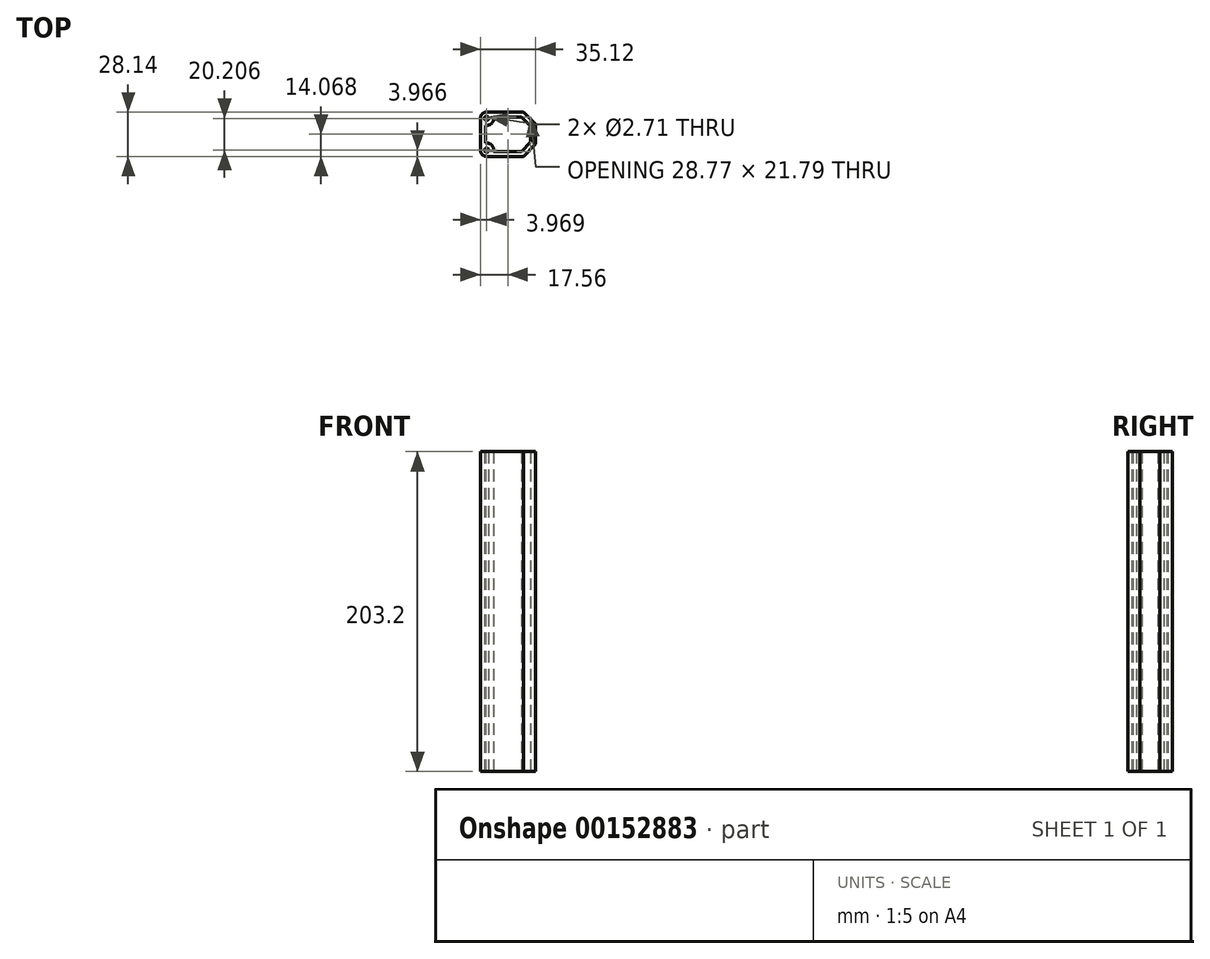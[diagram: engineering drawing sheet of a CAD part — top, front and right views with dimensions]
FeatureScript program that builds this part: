
annotation { "Feature Type Name" : "Feature", "Feature Type Description" : "" }
export const myFeature = defineFeature(function(context is Context, id is Id, definition is map)
    precondition{}
    {
        {
            var Q0;
            Q0=qCreatedBy(makeId("Top.planeOp"),FACE);
            var sketch = newSketch(context, id + "F0", { "sketchPlane" : qUnion([Q0])});
            skCircle(sketch, "E0", {"center": v(3.97, -24.17) * mm, "radius": 1.35 * mm});
            skLineSegment(sketch, "E1", {"start": v(27.4, 0) * mm, "end": v(35.12, -7.72) * mm});
            skLineSegment(sketch, "E2", {"start": v(35.12, -7.72) * mm, "end": v(35.12, -20.42) * mm});
            skLineSegment(sketch, "E3", {"start": v(35.12, -20.42) * mm, "end": v(27.4, -28.14) * mm});
            skCircle(sketch, "E4", {"center": v(3.97, -3.97) * mm, "radius": 1.35 * mm});
            skLineSegment(sketch, "E5", {"start": v(0, 0) * mm, "end": v(0, -28.14) * mm});
            skLineSegment(sketch, "E6", {"start": v(0, 0) * mm, "end": v(27.4, 0) * mm});
            skLineSegment(sketch, "E7", {"start": v(0, -28.14) * mm, "end": v(27.4, -28.14) * mm});
            skLineSegment(sketch, "E8", {"start": v(3.97, 0) * mm, "end": v(3.97, -3.97) * mm, "construction": true});
            skLineSegment(sketch, "E9", {"start": v(3.97, -3.97) * mm, "end": v(3.97, -24.17) * mm, "construction": true});
            skLineSegment(sketch, "E10", {"start": v(3.97, -24.17) * mm, "end": v(3.97, -28.14) * mm, "construction": true});
            skLineSegment(sketch, "E11", {"start": v(3.97, -14.07) * mm, "end": v(0, -14.07) * mm, "construction": true});
            skLineSegment(sketch, "E12", {"start": v(3.97, -14.07) * mm, "end": v(35.12, -14.07) * mm, "construction": true});
            skSolve(sketch);
        }
        {
            var Q0;
            Q0=qSketchRegion(id+"F0",true);
            extrude(context, id + "F1", {"entities" : qUnion([Q0]), "depth" : 203.2 * mm});
        }
        {
            var Q0;
            Q0=makeQuery(id+"F1.opExtrude","CAP_FACE",FACE,{"disambiguationData":[OSD([sQuery(id+"F0.wireOp",EDGE,"XEPYvsBn-YUR1-ND3i-Hliu-0bTDEalwyczA.top"),sQuery(id+"F0.wireOp",EDGE,"XEPYvsBn-YUR1-ND3i-Hliu-0bTDEalwyczA.left"),sQuery(id+"F0.wireOp",EDGE,"XEPYvsBn-YUR1-ND3i-Hliu-0bTDEalwyczA.right"),sQuery(id+"F0.wireOp",EDGE,"xVlwOPhJ-aCTn-OcWs-i2q0-JGyUUewlvZk0"),sQuery(id+"F0.wireOp",EDGE,"mnWjOHlk-ZBn2-aH8g-XAYR-hhn7P80mJV30"),sQuery(id+"F0.wireOp",EDGE,"qWcisiEL-inPN-Vpot-oWrz-rQQv9aT1plas"),sQuery(id+"F0.wireOp",EDGE,"E0"),sQuery(id+"F0.wireOp",EDGE,"wggGBD89-NySP-fc97-dHrN-DnFs8bvNLK9Q"),sQuery(id+"F0.wireOp",EDGE,"5MgdVyr7-DWw4-W8FQ-cNCn-mxH1OUoo9ziA"),sQuery(id+"F0.wireOp",EDGE,"vNbRmb8h-Bngh-6YxP-lEbM-9A7OkrAi9S9c"),sQuery(id+"F0.wireOp",EDGE,"E1"),sQuery(id+"F0.wireOp",EDGE,"E2"),sQuery(id+"F0.wireOp",EDGE,"E3"),sQuery(id+"F0.wireOp",EDGE,"jR9S6iYZ-1zVe-prUs-f2vK-9AuAnzNDGjG4"),sQuery(id+"F0.wireOp",EDGE,"E4"),sQuery(id+"F0.wireOp",EDGE,"pcKUxt8c-gCmA-zyht-Zhnu-jqMgmv6wgrW5")])],"isStart":false});
            shell(context, id + "F2", {"entities" : qUnion([Q0]), "thickness" : 3.17 * mm});
        }
        {
            var Q0;
            Q0=makeQuery(id+"F2.opShell","OFFSET_FACE",FACE,{"disambiguationData":[OSD([sQuery(id+"F0.wireOp",EDGE,"mnWjOHlk-ZBn2-aH8g-XAYR-hhn7P80mJV30"),sQuery(id+"F0.wireOp",EDGE,"qWcisiEL-inPN-Vpot-oWrz-rQQv9aT1plas"),sQuery(id+"F0.wireOp",EDGE,"E0"),sQuery(id+"F0.wireOp",EDGE,"wggGBD89-NySP-fc97-dHrN-DnFs8bvNLK9Q"),sQuery(id+"F0.wireOp",EDGE,"5MgdVyr7-DWw4-W8FQ-cNCn-mxH1OUoo9ziA"),sQuery(id+"F0.wireOp",EDGE,"vNbRmb8h-Bngh-6YxP-lEbM-9A7OkrAi9S9c"),sQuery(id+"F0.wireOp",EDGE,"E1"),sQuery(id+"F0.wireOp",EDGE,"E2"),sQuery(id+"F0.wireOp",EDGE,"E3"),sQuery(id+"F0.wireOp",EDGE,"jR9S6iYZ-1zVe-prUs-f2vK-9AuAnzNDGjG4"),sQuery(id+"F0.wireOp",EDGE,"E4"),sQuery(id+"F0.wireOp",EDGE,"pcKUxt8c-gCmA-zyht-Zhnu-jqMgmv6wgrW5")])]});
            var Q1;
            Q1=makeQuery(id+"F1.opExtrude","CAP_FACE",FACE,{"disambiguationData":[OSD([sQuery(id+"F0.wireOp",EDGE,"mnWjOHlk-ZBn2-aH8g-XAYR-hhn7P80mJV30"),sQuery(id+"F0.wireOp",EDGE,"qWcisiEL-inPN-Vpot-oWrz-rQQv9aT1plas"),sQuery(id+"F0.wireOp",EDGE,"E0"),sQuery(id+"F0.wireOp",EDGE,"wggGBD89-NySP-fc97-dHrN-DnFs8bvNLK9Q"),sQuery(id+"F0.wireOp",EDGE,"5MgdVyr7-DWw4-W8FQ-cNCn-mxH1OUoo9ziA"),sQuery(id+"F0.wireOp",EDGE,"vNbRmb8h-Bngh-6YxP-lEbM-9A7OkrAi9S9c"),sQuery(id+"F0.wireOp",EDGE,"E1"),sQuery(id+"F0.wireOp",EDGE,"E2"),sQuery(id+"F0.wireOp",EDGE,"E3"),sQuery(id+"F0.wireOp",EDGE,"jR9S6iYZ-1zVe-prUs-f2vK-9AuAnzNDGjG4"),sQuery(id+"F0.wireOp",EDGE,"E4"),sQuery(id+"F0.wireOp",EDGE,"pcKUxt8c-gCmA-zyht-Zhnu-jqMgmv6wgrW5")])],"isStart":true});
            extrude(context, id + "F3", {"entities" : qUnion([Q0]), "operationType" : NewBodyOperationType.REMOVE, "endBound" : BoundingType.UP_TO_SURFACE, "oppositeDirection" : true, "endBoundEntityFace" : qUnion([Q1]), "depth" : 25.4 * mm});
        }
        {
            var Q0;
            Q0=makeQuery(id+"F1.opExtrude","SWEPT_EDGE",EDGE,{"disambiguationData":[OSD([sQuery(id+"F0.wireOp",EDGE,"E5"),sQuery(id+"F0.wireOp",EDGE,"E6")])]});
            var Q1;
            Q1=makeQuery(id+"F1.opExtrude","SWEPT_EDGE",EDGE,{"disambiguationData":[OSD([sQuery(id+"F0.wireOp",EDGE,"E5"),sQuery(id+"F0.wireOp",EDGE,"E7")])]});
            fillet(context, id + "F4", {"entities" : qUnion([Q0, Q1]), "radius" : 3.97 * mm, "tangentPropagation" : true, "allowEdgeOverflow" : false});
        }
    });
